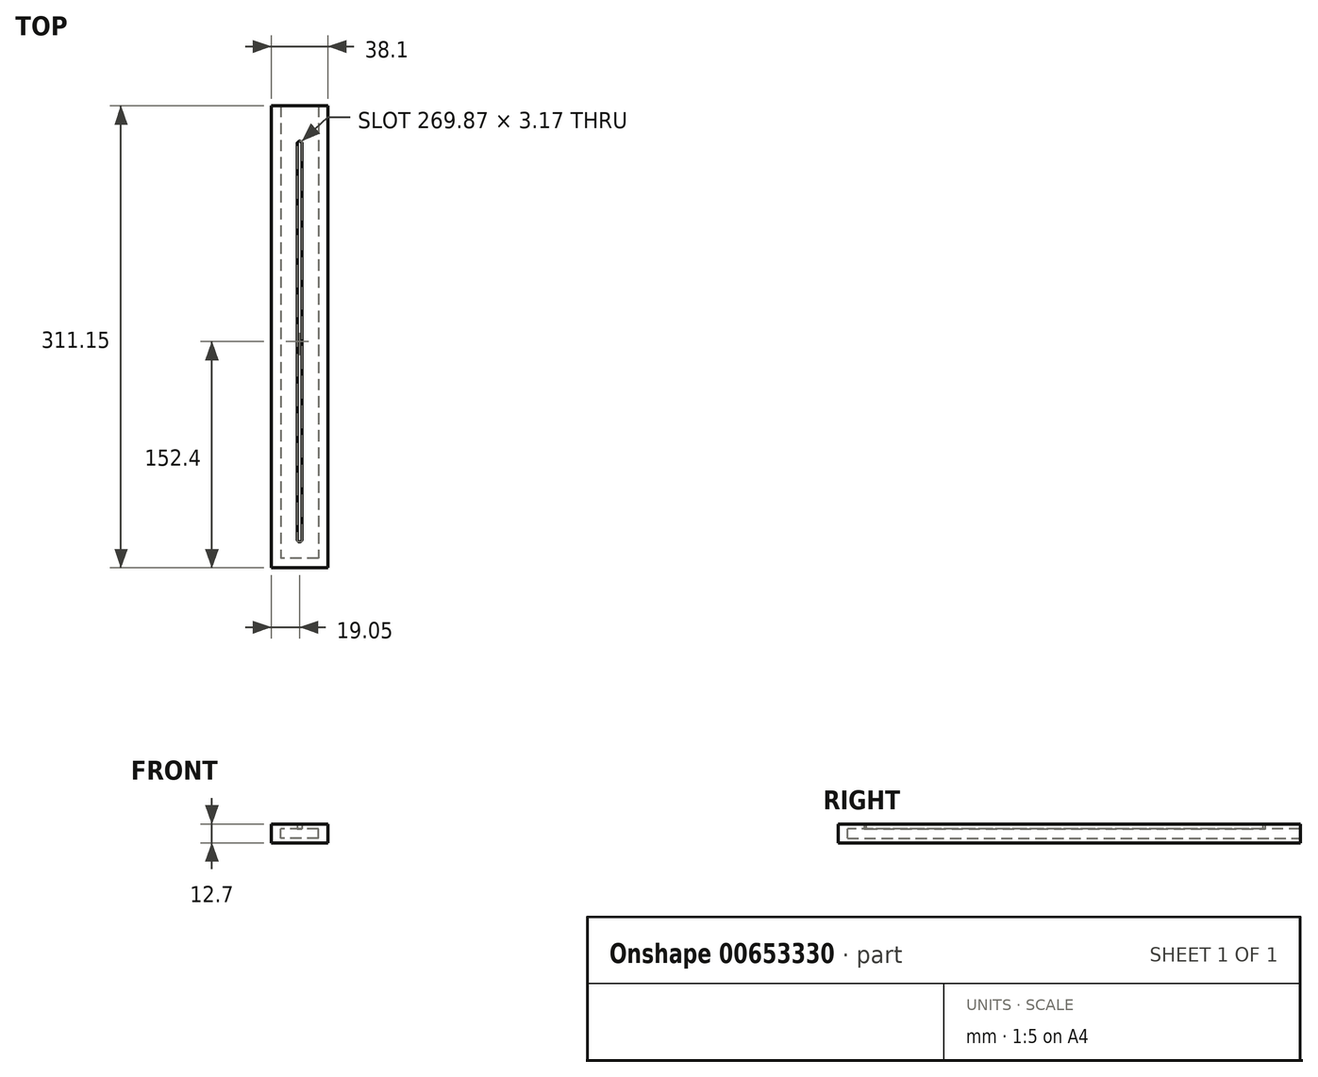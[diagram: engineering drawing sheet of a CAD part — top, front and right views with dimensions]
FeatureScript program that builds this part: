
annotation { "Feature Type Name" : "Feature", "Feature Type Description" : "" }
export const myFeature = defineFeature(function(context is Context, id is Id, definition is map)
    precondition{}
    {
        {
            var Q0;
            Q0=qCreatedBy(makeId("Top.planeOp"),FACE);
            var sketch = newSketch(context, id + "F0", { "sketchPlane" : qUnion([Q0])});
            skLineSegment(sketch, "E0.bottom", {"start": v(19.05, -152.4) * mm, "end": v(-19.05, -152.4) * mm});
            skLineSegment(sketch, "E0.top", {"start": v(19.05, 152.4) * mm, "end": v(-19.05, 152.4) * mm});
            skLineSegment(sketch, "E0.left", {"start": v(19.05, -152.4) * mm, "end": v(19.05, 152.4) * mm});
            skLineSegment(sketch, "E0.right", {"start": v(-19.05, -152.4) * mm, "end": v(-19.05, 152.4) * mm});
            skPoint(sketch, "E0.middle", {"position": v(0, 0) * mm});
            skSolve(sketch);
        }
        {
            var Q0;
            Q0 = qSketchRegion(id + "F0", true);
            extrude(context, id + "F1", {"entities" : qUnion([Q0]), "depth" : 3.17 * mm, "offsetDistance" : 25.4 * mm});
        }
        {
            var Q0;
            Q0=qCreatedBy(makeId("Right.planeOp"),FACE);
            var sketch = newSketch(context, id + "F2", { "sketchPlane" : qUnion([Q0])});
            skPoint(sketch, "E1.left.start.orphan", {"position": v(42.66, 0) * mm});
            skLineSegment(sketch, "E2.bottom", {"start": v(-152.4, 3.18) * mm, "end": v(152.4, 3.18) * mm});
            skLineSegment(sketch, "E2.top", {"start": v(-152.4, 12.7) * mm, "end": v(152.4, 12.7) * mm});
            skLineSegment(sketch, "E2.left", {"start": v(-152.4, 3.18) * mm, "end": v(-152.4, 12.7) * mm});
            skLineSegment(sketch, "E2.right", {"start": v(152.4, 3.17) * mm, "end": v(152.4, 12.7) * mm});
            skSolve(sketch);
        }
        {
            var Q0;
            Q0 = qSketchRegion(id + "F2", true);
            extrude(context, id + "F3", {"entities" : qUnion([Q0]), "operationType" : NewBodyOperationType.ADD, "depth" : 19.05 * mm, "offsetDistance" : 25.4 * mm, "hasSecondDirection" : true, "secondDirectionOppositeDirection" : false, "secondDirectionDepth" : 12.7 * mm});
        }
        {
            var Q0;
            Q0=makeQuery(id+"F2.imprint","IMPRINT",FACE,{"disambiguationData":[TD([[makeQuery(id+"F2.imprint","IMPRINT",EDGE,{"derivedFrom":sQuery(id+"F2.wireOp",EDGE,"E2.bottom")}),1.0]])]});
            extrude(context, id + "F4", {"entities" : qUnion([Q0]), "operationType" : NewBodyOperationType.ADD, "oppositeDirection" : true, "depth" : 19.05 * mm, "offsetDistance" : 25.4 * mm, "hasSecondDirection" : true, "secondDirectionOppositeDirection" : true, "secondDirectionDepth" : 12.7 * mm});
        }
        {
            var Q0;
            Q0=qCreatedBy(makeId("Front.planeOp"),FACE);
            var sketch = newSketch(context, id + "F5", { "sketchPlane" : qUnion([Q0])});
            skLineSegment(sketch, "E3.bottom", {"start": v(-19.05, 0) * mm, "end": v(19.05, 0) * mm});
            skLineSegment(sketch, "E3.top", {"start": v(-19.05, 12.7) * mm, "end": v(19.05, 12.7) * mm});
            skLineSegment(sketch, "E3.left", {"start": v(-19.05, 0) * mm, "end": v(-19.05, 12.7) * mm});
            skLineSegment(sketch, "E3.right", {"start": v(19.05, 0) * mm, "end": v(19.05, 12.7) * mm});
            skSolve(sketch);
        }
        {
            var Q0;
            Q0 = qSketchRegion(id + "F5", true);
            extrude(context, id + "F6", {"entities" : qUnion([Q0]), "operationType" : NewBodyOperationType.ADD, "depth" : 158.75 * mm, "offsetDistance" : 25.4 * mm, "hasSecondDirection" : true, "secondDirectionOppositeDirection" : false, "secondDirectionDepth" : 152.4 * mm});
        }
        {
            var Q0;
            Q0=qCreatedBy(makeId("Top.planeOp"),FACE);
            var sketch = newSketch(context, id + "F7", { "sketchPlane" : qUnion([Q0])});
            skLineSegment(sketch, "E4.bottom", {"start": v(-19.05, 152.4) * mm, "end": v(19.05, 152.4) * mm});
            skLineSegment(sketch, "E4.top", {"start": v(-19.05, -158.75) * mm, "end": v(19.05, -158.75) * mm});
            skLineSegment(sketch, "E4.left", {"start": v(-19.05, 152.4) * mm, "end": v(-19.05, -158.75) * mm});
            skLineSegment(sketch, "E4.right", {"start": v(19.05, 152.4) * mm, "end": v(19.05, -158.75) * mm});
            skArc(sketch, "E5", {"start": v(1.59, -139.71) * mm, "mid": v(0.02, -141.29) * mm, "end": v(-1.59, -139.76) * mm});
            skArc(sketch, "E6", {"start": v(1.58, 127.11) * mm, "mid": v(0, 128.59) * mm, "end": v(-1.58, 127.13) * mm});
            skLineSegment(sketch, "E7", {"start": v(-1.58, 127.13) * mm, "end": v(-1.59, -139.76) * mm});
            skLineSegment(sketch, "E8", {"start": v(1.59, -139.71) * mm, "end": v(1.58, 127.11) * mm});
            skSolve(sketch);
        }
        {
            var Q0;
            Q0=makeQuery(id+"F7.imprint","IMPRINT",FACE,{"disambiguationData":[TD([[makeQuery(id+"F7.imprint","IMPRINT",EDGE,{"derivedFrom":sQuery(id+"F7.wireOp",EDGE,"E4.bottom")}),-1.0]])]});
            extrude(context, id + "F8", {"entities" : qUnion([Q0]), "operationType" : NewBodyOperationType.ADD, "depth" : 12.7 * mm, "offsetDistance" : 25.4 * mm, "hasSecondDirection" : true, "secondDirectionOppositeDirection" : false, "secondDirectionDepth" : 9.52 * mm});
        }
    });
